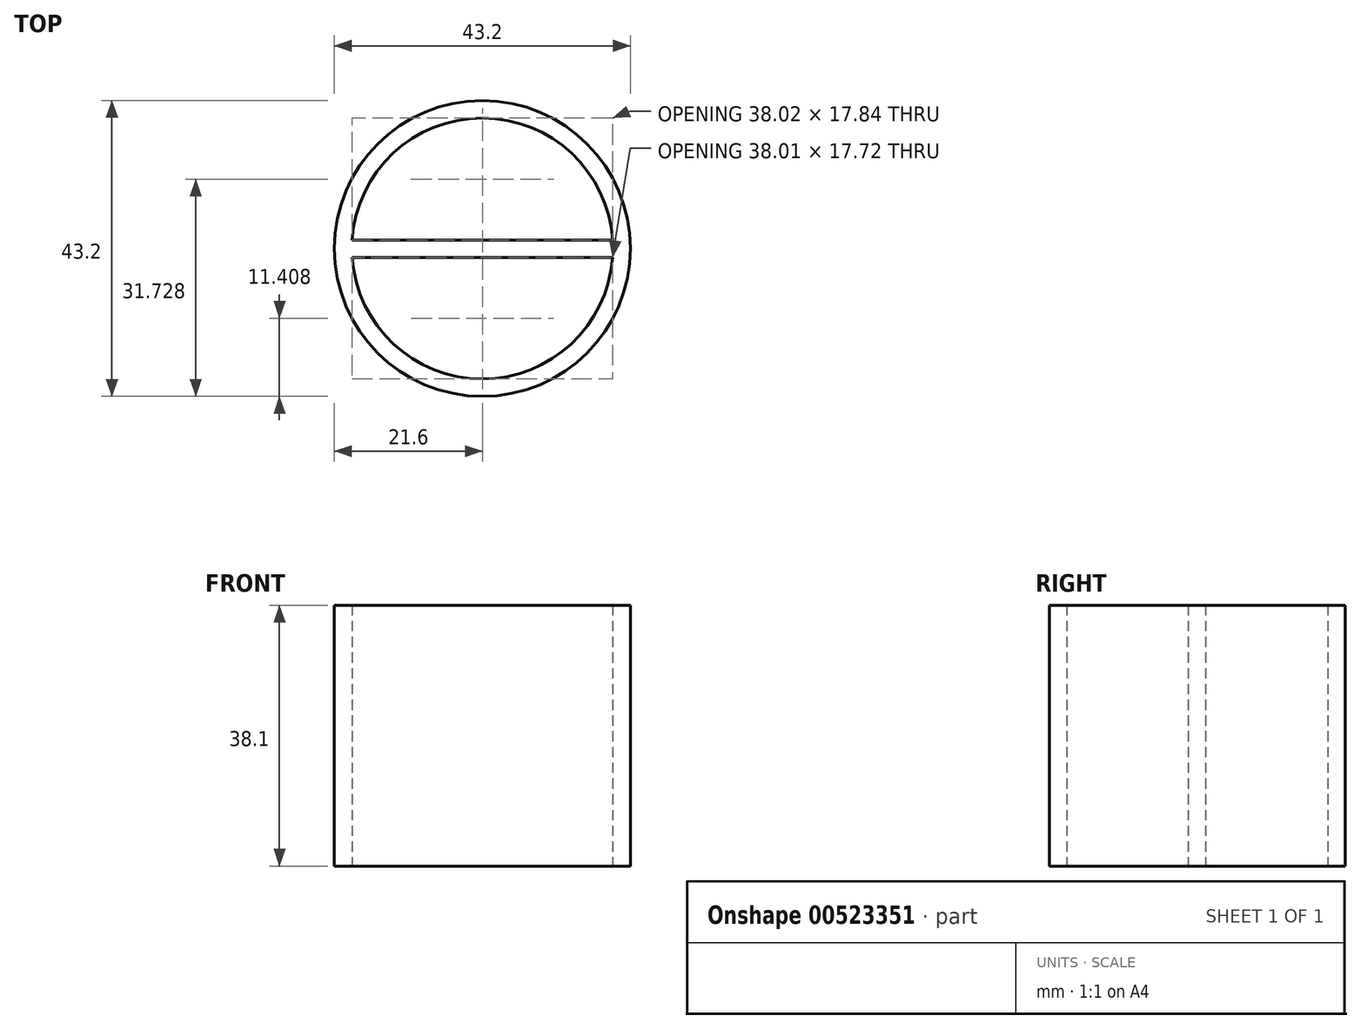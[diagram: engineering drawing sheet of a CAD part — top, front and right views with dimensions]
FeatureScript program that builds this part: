
annotation { "Feature Type Name" : "Feature", "Feature Type Description" : "" }
export const myFeature = defineFeature(function(context is Context, id is Id, definition is map)
    precondition{}
    {
        {
            var Q0;
            Q0=qCreatedBy(makeId("Top.planeOp"),FACE);
            var sketch = newSketch(context, id + "F0", { "sketchPlane" : qUnion([Q0])});
            skCircle(sketch, "E0", {"center": v(0, 0) * mm, "radius": 19.05 * mm});
            skCircle(sketch, "E1", {"center": v(0, 0) * mm, "radius": 21.6 * mm});
            skSolve(sketch);
        }
        {
            var Q0;
            Q0=makeQuery(id+"F0.imprint","IMPRINT",FACE,{"disambiguationData":[TD([[makeQuery(id+"F0.imprint","IMPRINT",EDGE,{"derivedFrom":sQuery(id+"F0.wireOp",EDGE,"E0")}),1.0]])]});
            var Q1;
            Q1=makeQuery(id+"F0.imprint","IMPRINT",FACE,{"disambiguationData":[TD([[makeQuery(id+"F0.imprint","IMPRINT",EDGE,{"derivedFrom":sQuery(id+"F0.wireOp",EDGE,"E0")}),-1.0]])]});
            var Q2;
            Q2=sQuery(id+"F0.wireOp",EDGE,"E0");
            var Q3;
            Q3=sQuery(id+"F0.wireOp",EDGE,"E1");
            extrude(context, id + "F1", {"entities" : qUnion([Q0, Q1]), "surfaceEntities" : qUnion([Q2, Q3]), "depth" : 38.1 * mm, "offsetDistance" : 25.4 * mm});
        }
        {
            var Q0;
            Q0=makeQuery(id+"F0.imprint","IMPRINT",FACE,{"disambiguationData":[TD([[makeQuery(id+"F0.imprint","IMPRINT",EDGE,{"derivedFrom":sQuery(id+"F0.wireOp",EDGE,"E0")}),1.0]])]});
            extrude(context, id + "F2", {"entities" : qUnion([Q0]), "operationType" : NewBodyOperationType.REMOVE, "depth" : 76.2 * mm, "offsetDistance" : 25.4 * mm});
        }
        {
            var Q0;
            Q0=makeQuery(id+"F0.imprint","IMPRINT",FACE,{"disambiguationData":[TD([[makeQuery(id+"F0.imprint","IMPRINT",EDGE,{"derivedFrom":sQuery(id+"F0.wireOp",EDGE,"E0")}),1.0]])]});
            var sketch = newSketch(context, id + "F3", { "sketchPlane" : qUnion([Q0])});
            skLineSegment(sketch, "E2.bottom", {"start": v(-20.29, 1.2) * mm, "end": v(19.99, 1.2) * mm});
            skLineSegment(sketch, "E2.top", {"start": v(-20.29, -1.33) * mm, "end": v(19.99, -1.33) * mm});
            skLineSegment(sketch, "E2.left", {"start": v(-20.29, 1.2) * mm, "end": v(-20.29, -1.33) * mm});
            skLineSegment(sketch, "E2.right", {"start": v(19.99, 1.2) * mm, "end": v(19.99, -1.33) * mm});
            skSolve(sketch);
        }
        {
            var Q0;
            Q0 = qSketchRegion(id + "F3", true);
            extrude(context, id + "F4", {"entities" : qUnion([Q0]), "operationType" : NewBodyOperationType.ADD, "depth" : 38.1 * mm, "offsetDistance" : 25.4 * mm});
        }
    });
